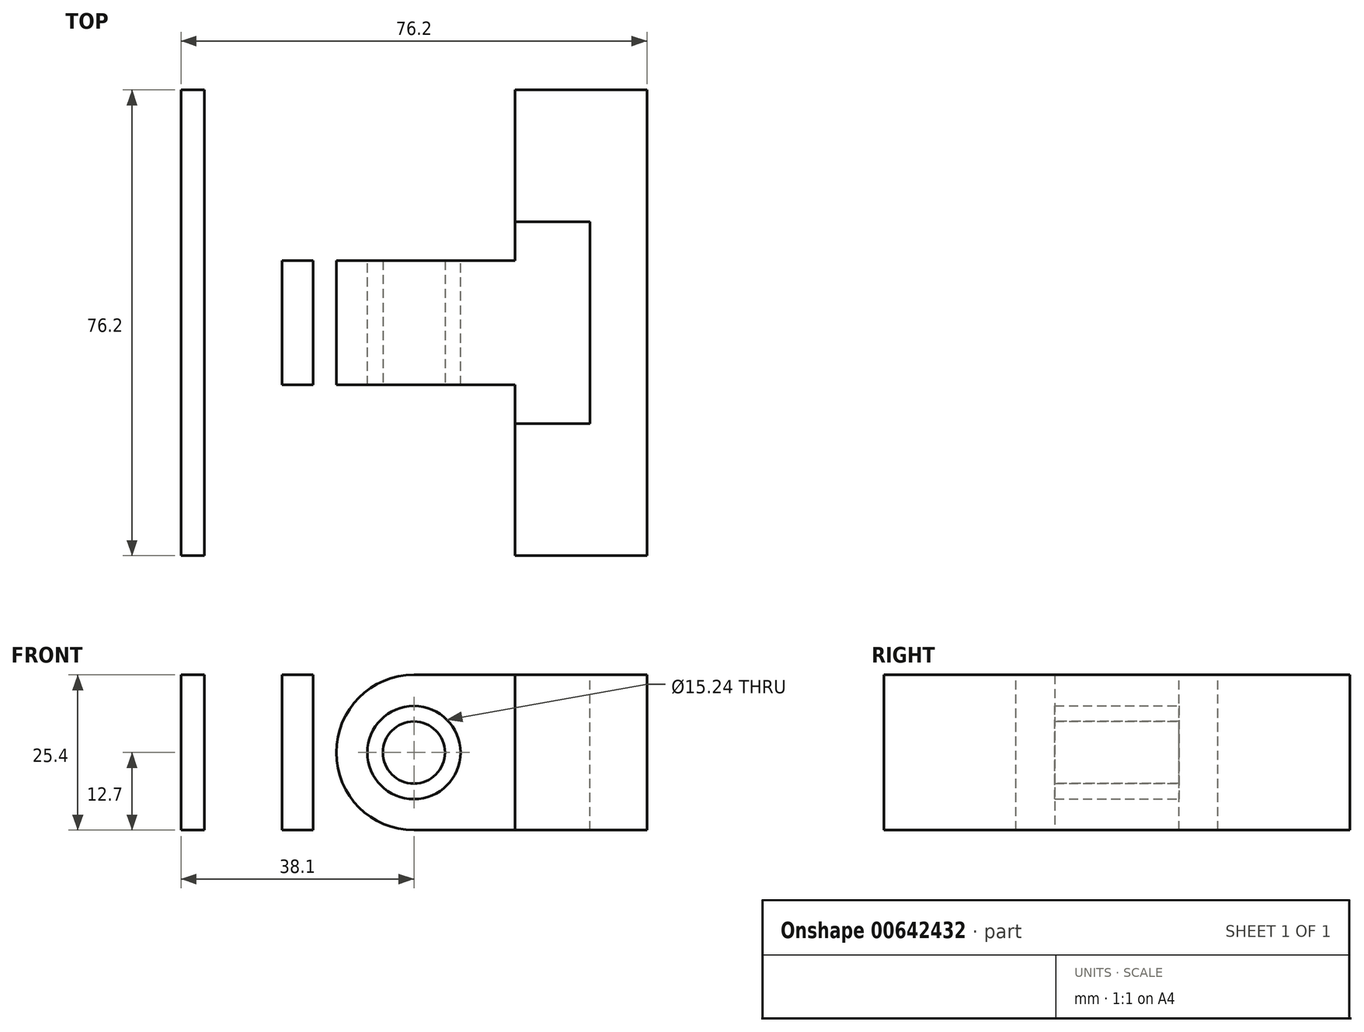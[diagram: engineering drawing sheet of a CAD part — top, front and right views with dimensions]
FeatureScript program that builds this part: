
annotation { "Feature Type Name" : "Feature", "Feature Type Description" : "" }
export const myFeature = defineFeature(function(context is Context, id is Id, definition is map)
    precondition{}
    {
        {
            var Q0;
            Q0=qCreatedBy(makeId("Front.planeOp"),FACE);
            var sketch = newSketch(context, id + "F0", { "sketchPlane" : qUnion([Q0])});
            skLineSegment(sketch, "E0", {"start": v(-12.7, 12.7) * mm, "end": v(38.1, 12.7) * mm});
            skLineSegment(sketch, "E1", {"start": v(38.1, 12.7) * mm, "end": v(38.1, -12.7) * mm});
            skLineSegment(sketch, "E2", {"start": v(38.1, -12.7) * mm, "end": v(-12.7, -12.7) * mm});
            skLineSegment(sketch, "E3", {"start": v(-12.7, -12.7) * mm, "end": v(-12.7, 12.7) * mm});
            skSolve(sketch);
        }
        {
            var Q0;
            Q0=makeQuery(id+"F0.imprint","IMPRINT",FACE,{"disambiguationData":[TD([[makeQuery(id+"F0.imprint","IMPRINT",EDGE,{"derivedFrom":sQuery(id+"F0.wireOp",EDGE,"E0")}),-1.0]])]});
            extrude(context, id + "F1", {"entities" : qUnion([Q0]), "oppositeDirection" : true, "depth" : 76.2 * mm, "offsetDistance" : 25.4 * mm});
        }
        {
            var Q0;
            Q0=makeQuery(id+"F1.opExtrude","SWEPT_EDGE",EDGE,{"disambiguationData":[OSD([sQuery(id+"F0.wireOp",EDGE,"E0"),sQuery(id+"F0.wireOp",EDGE,"E1")])]});
            var Q1;
            Q1=makeQuery(id+"F1.opExtrude","SWEPT_EDGE",EDGE,{"disambiguationData":[OSD([sQuery(id+"F0.wireOp",EDGE,"E1"),sQuery(id+"F0.wireOp",EDGE,"E2")])]});
            fillet(context, id + "F2", {"entities" : qUnion([Q0, Q1]), "radius" : 12.7 * mm, "tangentPropagation" : true, "allowEdgeOverflow" : false});
        }
        {
            var Q0;
            Q0=makeQuery(id+"F1.opExtrude","SWEPT_FACE",FACE,{"disambiguationData":[OSD([sQuery(id+"F0.wireOp",EDGE,"E0")])]});
            var sketch = newSketch(context, id + "F3", { "sketchPlane" : qUnion([Q0])});
            skLineSegment(sketch, "E4.bottom", {"start": v(8.9, 21.59) * mm, "end": v(54.2, 21.59) * mm});
            skLineSegment(sketch, "E4.top", {"start": v(8.89, 54.61) * mm, "end": v(54.2, 54.61) * mm});
            skLineSegment(sketch, "E4.left", {"start": v(8.9, 21.59) * mm, "end": v(8.89, 54.61) * mm});
            skLineSegment(sketch, "E4.right", {"start": v(54.2, 21.59) * mm, "end": v(54.2, 54.61) * mm});
            skPoint(sketch, "E4.middle", {"position": v(31.55, 38.1) * mm});
            skSolve(sketch);
        }
        {
            var Q0;
            {var subQ0=sQuery(id+"F3.wireOp",EDGE,"E4.right");Q0=makeQuery(id+"F3.imprint","IMPRINT",FACE,{"disambiguationData":[TD([[makeQuery(id+"F3.imprint","IMPRINT",EDGE,{"derivedFrom":subQ0}),1.0]])]});}
            var Q1;
            {var subQ0=sQuery(id+"F3.wireOp",EDGE,"E4.left");Q1=makeQuery(id+"F3.imprint","IMPRINT",FACE,{"disambiguationData":[TD([[makeQuery(id+"F3.imprint","IMPRINT",EDGE,{"derivedFrom":subQ0}),-1.0]])]});}
            extrude(context, id + "F4", {"entities" : qUnion([Q0, Q1]), "operationType" : NewBodyOperationType.REMOVE, "oppositeDirection" : true, "depth" : 25.4 * mm, "offsetDistance" : 25.4 * mm});
        }
        {
            var Q0;
            Q0=makeQuery(id+"F4.boolean.opBoolean","COPY",FACE,{"derivedFrom":makeQuery(id+"F4.opExtrude","SWEPT_FACE",FACE,{"disambiguationData":[OSD([sQuery(id+"F3.wireOp",EDGE,"E4.bottom")])]})});
            var sketch = newSketch(context, id + "F5", { "sketchPlane" : qUnion([Q0])});
            skCircle(sketch, "E5", {"center": v(-25.4, 0) * mm, "radius": 5.08 * mm});
            skSolve(sketch);
        }
        {
            var Q0;
            Q0 = qSketchRegion(id + "F5", true);
            extrude(context, id + "F6", {"entities" : qUnion([Q0]), "operationType" : NewBodyOperationType.ADD, "depth" : 34.2 * mm, "offsetDistance" : 25.4 * mm});
        }
        {
            var Q0;
            Q0=qCreatedBy(makeId("Front.planeOp"),FACE);
            var sketch = newSketch(context, id + "F7", { "sketchPlane" : qUnion([Q0])});
            skLineSegment(sketch, "E6.bottom", {"start": v(12.7, 12.7) * mm, "end": v(63.5, 12.7) * mm});
            skLineSegment(sketch, "E6.top", {"start": v(12.7, -12.7) * mm, "end": v(63.5, -12.7) * mm});
            skLineSegment(sketch, "E6.left", {"start": v(12.7, 12.7) * mm, "end": v(12.7, -12.7) * mm});
            skLineSegment(sketch, "E6.right", {"start": v(63.5, 12.7) * mm, "end": v(63.5, -12.7) * mm});
            skSolve(sketch);
        }
        {
            var Q0;
            Q0=makeQuery(id+"F7.imprint","IMPRINT",FACE,{"disambiguationData":[TD([[makeQuery(id+"F7.imprint","IMPRINT",EDGE,{"derivedFrom":sQuery(id+"F7.wireOp",EDGE,"E6.bottom")}),-1.0]])]});
            extrude(context, id + "F8", {"entities" : qUnion([Q0]), "oppositeDirection" : true, "depth" : 76.2 * mm, "offsetDistance" : 25.4 * mm});
        }
        {
            var Q0;
            Q0=makeQuery(id+"F8.opExtrude","SWEPT_FACE",FACE,{"disambiguationData":[OSD([sQuery(id+"F7.wireOp",EDGE,"E6.bottom")])]});
            var sketch = newSketch(context, id + "F9", { "sketchPlane" : qUnion([Q0])});
            skLineSegment(sketch, "E7", {"start": v(41.91, 78.74) * mm, "end": v(41.91, 48.26) * mm});
            skLineSegment(sketch, "E8", {"start": v(41.91, 48.26) * mm, "end": v(3.81, 48.26) * mm});
            skLineSegment(sketch, "E9", {"start": v(3.81, 48.26) * mm, "end": v(3.81, 27.94) * mm});
            skLineSegment(sketch, "E10", {"start": v(3.81, 27.94) * mm, "end": v(41.91, 27.94) * mm});
            skLineSegment(sketch, "E11", {"start": v(41.91, 27.94) * mm, "end": v(41.91, -2.54) * mm});
            skLineSegment(sketch, "E12", {"start": v(41.91, -2.54) * mm, "end": v(-8.9, -2.54) * mm});
            skLineSegment(sketch, "E13", {"start": v(-8.9, -2.54) * mm, "end": v(-8.9, 78.74) * mm});
            skLineSegment(sketch, "E14", {"start": v(-8.9, 78.74) * mm, "end": v(41.91, 78.74) * mm});
            skSolve(sketch);
        }
        {
            var Q0;
            {var subQ0=sQuery(id+"F9.wireOp",EDGE,"E8");var subQ1=sQuery(id+"F9.wireOp",EDGE,"E7");var subQ2=makeQuery(id+"F9.imprint","INTERSECT",VERTEX,{"derivedFrom":[subQ1,subQ0]});Q0=makeQuery(id+"F9.imprint","IMPRINT",FACE,{"disambiguationData":[TD([[makeQuery(id+"F9.imprint","IMPRINT",EDGE,{"disambiguationData":[TD([[subQ2,1.0]])],"derivedFrom":subQ1}),-1.0]])]});}
            var Q1;
            {var subQ13=sQuery(id+"F9.wireOp",EDGE,"E9");Q1=makeQuery(id+"F9.imprint","IMPRINT",FACE,{"disambiguationData":[TD([[makeQuery(id+"F9.imprint","IMPRINT",EDGE,{"derivedFrom":subQ13}),-1.0]])]});}
            var Q2;
            {var subQ0=sQuery(id+"F9.wireOp",EDGE,"E11");var subQ1=sQuery(id+"F9.wireOp",EDGE,"E10");var subQ2=makeQuery(id+"F9.imprint","INTERSECT",VERTEX,{"derivedFrom":[subQ1,subQ0]});Q2=makeQuery(id+"F9.imprint","IMPRINT",FACE,{"disambiguationData":[TD([[makeQuery(id+"F9.imprint","IMPRINT",EDGE,{"disambiguationData":[TD([[subQ2,-1.0]])],"derivedFrom":subQ0}),-1.0]])]});}
            extrude(context, id + "F10", {"entities" : qUnion([Q0, Q1, Q2]), "operationType" : NewBodyOperationType.REMOVE, "oppositeDirection" : true, "depth" : 25.4 * mm, "offsetDistance" : 25.4 * mm});
        }
        {
            var Q0;
            Q0=makeQuery(id+"F8.opExtrude","SWEPT_EDGE",EDGE,{"disambiguationData":[OSD([sQuery(id+"F7.wireOp",EDGE,"E6.bottom"),sQuery(id+"F7.wireOp",EDGE,"E6.left")])]});
            var Q1;
            Q1=makeQuery(id+"F8.opExtrude","SWEPT_EDGE",EDGE,{"disambiguationData":[OSD([sQuery(id+"F7.wireOp",EDGE,"E6.top"),sQuery(id+"F7.wireOp",EDGE,"E6.left")])]});
            fillet(context, id + "F11", {"entities" : qUnion([Q0, Q1]), "radius" : 12.7 * mm, "tangentPropagation" : true, "allowEdgeOverflow" : false});
        }
        {
            var Q0;
            Q0=makeQuery(id+"F10.boolean.opBoolean","COPY",FACE,{"derivedFrom":makeQuery(id+"F10.opExtrude","SWEPT_FACE",FACE,{"disambiguationData":[OSD([sQuery(id+"F9.wireOp",EDGE,"E8")])]})});
            var sketch = newSketch(context, id + "F12", { "sketchPlane" : qUnion([Q0])});
            skCircle(sketch, "E15", {"center": v(-25.4, 0) * mm, "radius": 7.62 * mm});
            skSolve(sketch);
        }
        {
            var Q0;
            Q0=makeQuery(id+"F12.imprint","IMPRINT",FACE,{"disambiguationData":[TD([[makeQuery(id+"F12.imprint","IMPRINT",EDGE,{"derivedFrom":sQuery(id+"F12.wireOp",EDGE,"E15")}),1.0]])]});
            extrude(context, id + "F13", {"entities" : qUnion([Q0]), "operationType" : NewBodyOperationType.REMOVE, "oppositeDirection" : true, "depth" : 25.4 * mm, "offsetDistance" : 25.4 * mm});
        }
    });
